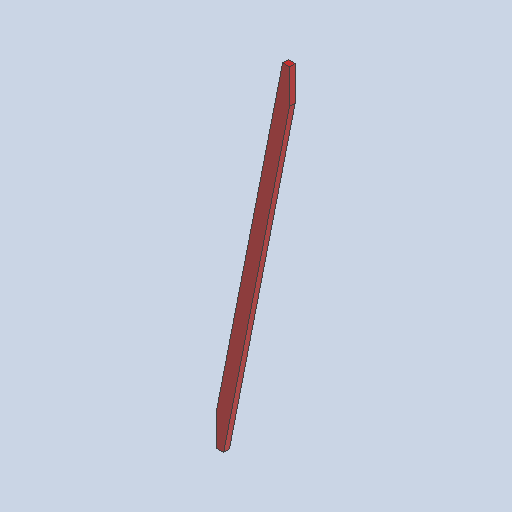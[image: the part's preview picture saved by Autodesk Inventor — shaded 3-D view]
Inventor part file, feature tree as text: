
AUTODESK INVENTOR PART (.ipt)
format: ipt  version: 2025.1 (Build 291241020, 241B)  size: 257,536 bytes
history: native  units: in
note: dims shown in document units (in); Inventor stores cm internally (conversion verified against a paired STEP export)
features: other x7, reference x4, extrude x1, sketch x1
ambient origin geometry x8: Origin, YZ Plane, XZ Plane, XY Plane, X Axis, Y Axis, Z Axis, Center Point
bodies: Solid1 (feature_tree)
feature tree (13):
  extrude  "Extrusion1"  [1 undecoded]
  sketch  "Sketch1"  dims[d2=1.5in d3=0.0in]
  reference  "Reference1"
  reference  "Reference2"
  reference  "Reference3"
  reference  "Reference4"
  other  "<userpath>\Documents\Tburn24\layer1\layer1.iam"
  other  "layer1.iam"
  other  "10'x2x4:8"
  other  "7'5x2x4:1"
  other  "10'x2x4:2"
  other  "7'5x2x4:8"
  other  "Finish1"
note: 1 required parameter value undecoded (feature->parameter linkage not recoverable at this tier; creation-order binding heuristic only, values carry confidence <= 0.55)
